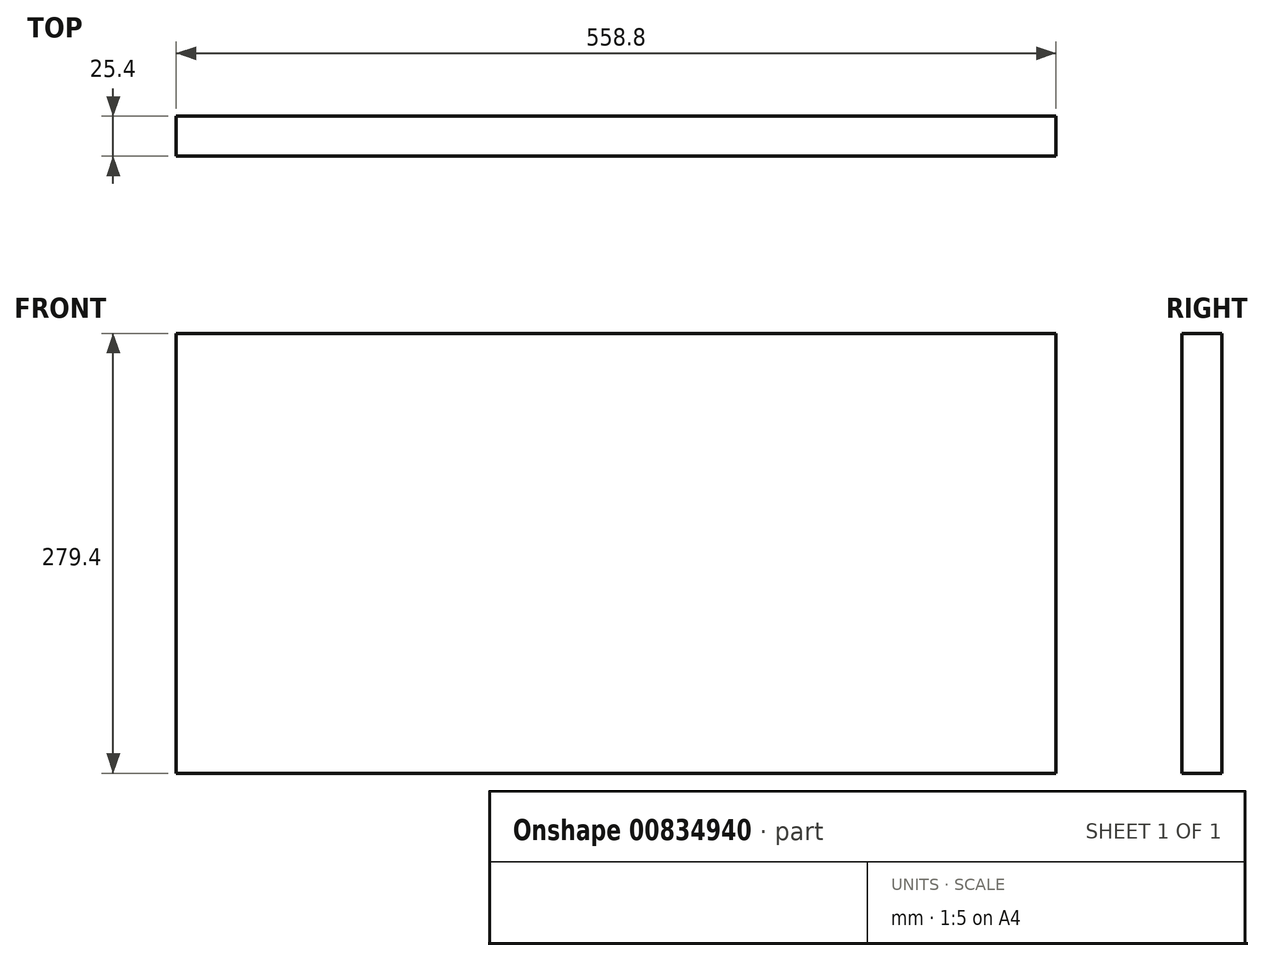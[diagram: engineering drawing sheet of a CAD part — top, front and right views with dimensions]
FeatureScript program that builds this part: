
annotation { "Feature Type Name" : "Feature", "Feature Type Description" : "" }
export const myFeature = defineFeature(function(context is Context, id is Id, definition is map)
    precondition{}
    {
        {
            var Q0;
            Q0=qCreatedBy(makeId("Front.planeOp"),FACE);
            var sketch = newSketch(context, id + "F0", { "sketchPlane" : qUnion([Q0])});
            skLineSegment(sketch, "E0.bottom", {"start": v(279.4, 139.7) * mm, "end": v(-279.4, 139.7) * mm});
            skLineSegment(sketch, "E0.top", {"start": v(279.4, -139.7) * mm, "end": v(-279.4, -139.7) * mm});
            skLineSegment(sketch, "E0.left", {"start": v(279.4, 139.7) * mm, "end": v(279.4, -139.7) * mm});
            skLineSegment(sketch, "E0.right", {"start": v(-279.4, 139.7) * mm, "end": v(-279.4, -139.7) * mm});
            skPoint(sketch, "E0.middle", {"position": v(0, 0) * mm});
            skSolve(sketch);
        }
        {
            var Q0;
            Q0 = qSketchRegion(id + "F0", true);
            extrude(context, id + "F1", {"entities" : qUnion([Q0]), "depth" : 25.4 * mm, "offsetDistance" : 25.4 * mm});
        }
    });
